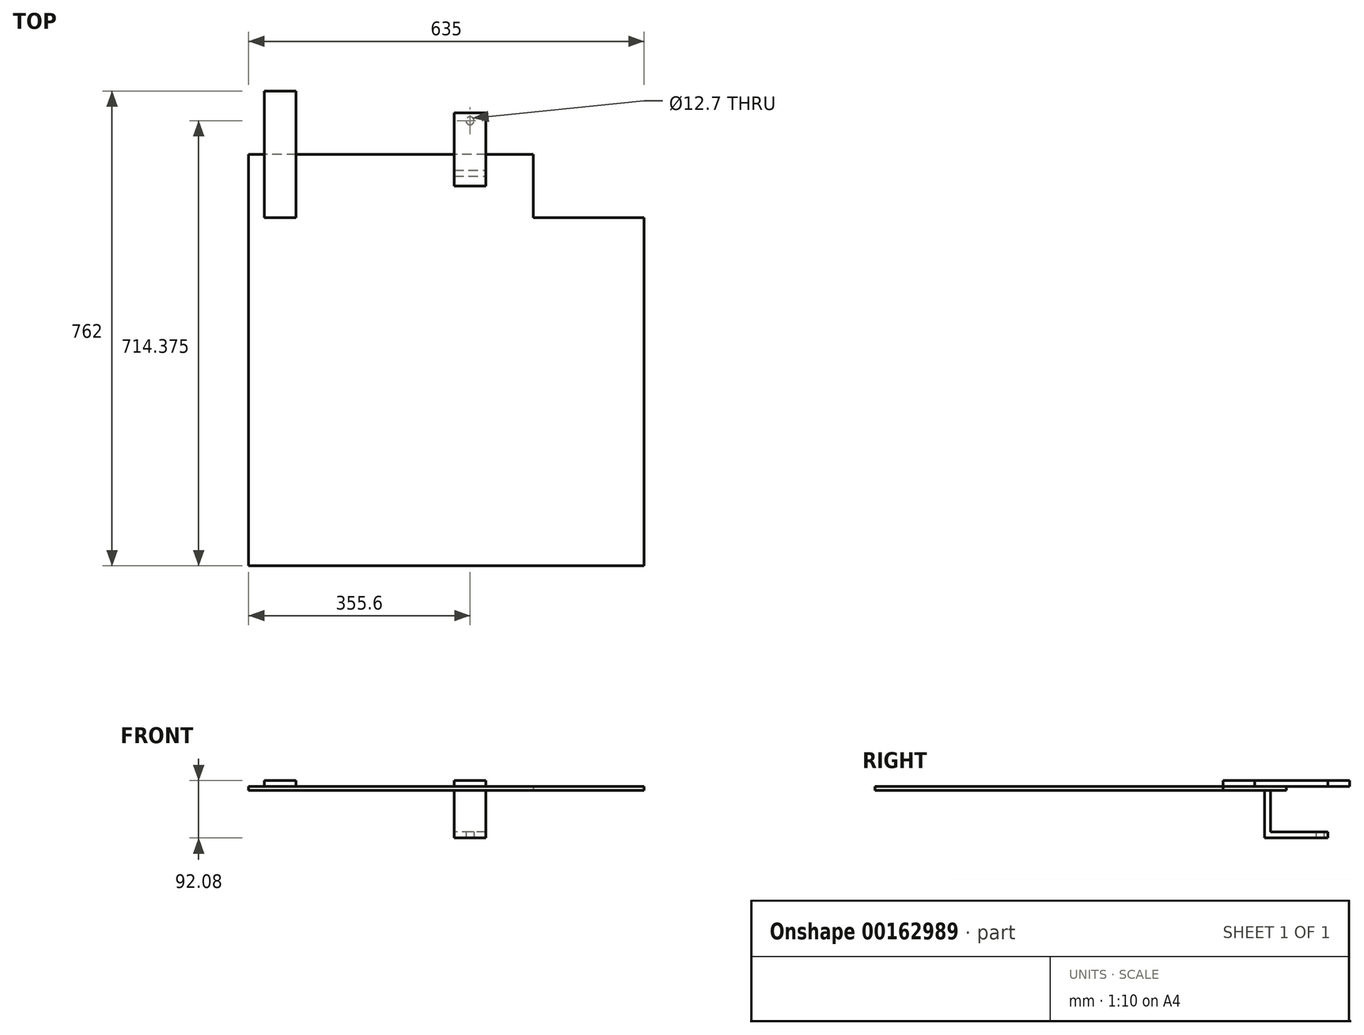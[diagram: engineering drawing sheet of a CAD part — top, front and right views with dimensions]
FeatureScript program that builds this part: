
annotation { "Feature Type Name" : "Feature", "Feature Type Description" : "" }
export const myFeature = defineFeature(function(context is Context, id is Id, definition is map)
    precondition{}
    {
        {
            var Q0;
            Q0=qCreatedBy(makeId("Top.planeOp"),FACE);
            var sketch = newSketch(context, id + "F0", { "sketchPlane" : qUnion([Q0])});
            skLineSegment(sketch, "E0.bottom", {"start": v(317.5, -330.2) * mm, "end": v(-317.5, -330.2) * mm});
            skLineSegment(sketch, "E0.top", {"start": v(139.7, 330.2) * mm, "end": v(-317.5, 330.2) * mm});
            skLineSegment(sketch, "E0.left", {"start": v(317.5, -330.2) * mm, "end": v(317.5, 228.6) * mm});
            skLineSegment(sketch, "E0.right", {"start": v(-317.5, -330.2) * mm, "end": v(-317.5, 330.2) * mm});
            skPoint(sketch, "E0.middle", {"position": v(0, 0) * mm});
            skLineSegment(sketch, "E1.top", {"start": v(317.5, 228.6) * mm, "end": v(139.7, 228.6) * mm});
            skLineSegment(sketch, "E1.right", {"start": v(139.7, 330.2) * mm, "end": v(139.7, 228.6) * mm});
            skPoint(sketch, "E2.orphan", {"position": v(317.5, 330.2) * mm});
            skSolve(sketch);
        }
        {
            var Q0;
            Q0=makeQuery(id+"F0.imprint","IMPRINT",FACE,{"disambiguationData":[TD([[makeQuery(id+"F0.imprint","IMPRINT",EDGE,{"derivedFrom":sQuery(id+"F0.wireOp",EDGE,"E0.bottom")}),-1.0]])]});
            extrude(context, id + "F1", {"entities" : qUnion([Q0]), "depth" : 6.35 * mm});
        }
        {
            var Q0;
            Q0=makeQuery(id+"F1.opExtrude","CAP_FACE",FACE,{"disambiguationData":[OSD([sQuery(id+"F0.wireOp",EDGE,"E0.bottom"),sQuery(id+"F0.wireOp",EDGE,"E0.top"),sQuery(id+"F0.wireOp",EDGE,"E0.left"),sQuery(id+"F0.wireOp",EDGE,"E0.right"),sQuery(id+"F0.wireOp",EDGE,"E1.top"),sQuery(id+"F0.wireOp",EDGE,"E1.right")])],"isStart":false});
            var sketch = newSketch(context, id + "F2", { "sketchPlane" : qUnion([Q0])});
            skLineSegment(sketch, "E3.bottom", {"start": v(-241.3, 228.6) * mm, "end": v(-292.1, 228.6) * mm});
            skLineSegment(sketch, "E3.top", {"start": v(-241.3, 431.8) * mm, "end": v(-292.1, 431.8) * mm});
            skLineSegment(sketch, "E3.left", {"start": v(-241.3, 228.6) * mm, "end": v(-241.3, 431.8) * mm});
            skLineSegment(sketch, "E3.right", {"start": v(-292.1, 228.6) * mm, "end": v(-292.1, 431.8) * mm});
            skPoint(sketch, "E3.middle", {"position": v(-266.7, 330.2) * mm});
            skSolve(sketch);
        }
        {
            var Q0;
            {var subQ0=sQuery(id+"F2.wireOp",EDGE,"E3.bottom");Q0=makeQuery(id+"F2.imprint","IMPRINT",FACE,{"disambiguationData":[TD([[makeQuery(id+"F2.imprint","IMPRINT",EDGE,{"derivedFrom":subQ0}),-1.0]])]});}
            var Q1;
            {var subQ0=sQuery(id+"F2.wireOp",EDGE,"E3.top");Q1=makeQuery(id+"F2.imprint","IMPRINT",FACE,{"disambiguationData":[TD([[makeQuery(id+"F2.imprint","IMPRINT",EDGE,{"derivedFrom":subQ0}),1.0]])]});}
            extrude(context, id + "F3", {"entities" : qUnion([Q0, Q1]), "operationType" : NewBodyOperationType.ADD, "depth" : 9.52 * mm});
        }
        {
            var Q0;
            Q0=makeQuery(id+"F1.opExtrude","CAP_FACE",FACE,{"disambiguationData":[OSD([sQuery(id+"F0.wireOp",EDGE,"E0.bottom"),sQuery(id+"F0.wireOp",EDGE,"E0.top"),sQuery(id+"F0.wireOp",EDGE,"E0.left"),sQuery(id+"F0.wireOp",EDGE,"E0.right"),sQuery(id+"F0.wireOp",EDGE,"E1.top"),sQuery(id+"F0.wireOp",EDGE,"E1.right")])],"isStart":true});
            var sketch = newSketch(context, id + "F4", { "sketchPlane" : qUnion([Q0])});
            skLineSegment(sketch, "E4.bottom", {"start": v(12.7, -295.28) * mm, "end": v(63.5, -295.28) * mm});
            skLineSegment(sketch, "E4.top", {"start": v(12.7, -304.8) * mm, "end": v(63.5, -304.8) * mm});
            skLineSegment(sketch, "E4.left", {"start": v(12.7, -295.28) * mm, "end": v(12.7, -304.8) * mm});
            skLineSegment(sketch, "E4.right", {"start": v(63.5, -295.28) * mm, "end": v(63.5, -304.8) * mm});
            skPoint(sketch, "E4.middle", {"position": v(38.1, -300.04) * mm});
            skSolve(sketch);
        }
        {
            var Q0;
            Q0=makeQuery(id+"F4.imprint","IMPRINT",FACE,{"disambiguationData":[TD([[makeQuery(id+"F4.imprint","IMPRINT",EDGE,{"derivedFrom":sQuery(id+"F4.wireOp",EDGE,"E4.bottom")}),-1.0]])]});
            extrude(context, id + "F5", {"entities" : qUnion([Q0]), "operationType" : NewBodyOperationType.ADD, "depth" : 76.2 * mm});
        }
        {
            var Q0;
            Q0=makeQuery(id+"F5.opExtrude","SWEPT_FACE",FACE,{"disambiguationData":[OSD([sQuery(id+"F4.wireOp",EDGE,"E4.top")])]});
            var sketch = newSketch(context, id + "F6", { "sketchPlane" : qUnion([Q0])});
            skLineSegment(sketch, "E5.bottom", {"start": v(-63.5, -76.2) * mm, "end": v(-12.7, -76.2) * mm});
            skLineSegment(sketch, "E5.top", {"start": v(-63.5, -66.68) * mm, "end": v(-12.7, -66.68) * mm});
            skLineSegment(sketch, "E5.left", {"start": v(-63.5, -76.2) * mm, "end": v(-63.5, -66.68) * mm});
            skLineSegment(sketch, "E5.right", {"start": v(-12.7, -76.2) * mm, "end": v(-12.7, -66.68) * mm});
            skSolve(sketch);
        }
        {
            var Q0;
            Q0=makeQuery(id+"F6.imprint","IMPRINT",FACE,{"disambiguationData":[TD([[makeQuery(id+"F6.imprint","IMPRINT",EDGE,{"derivedFrom":sQuery(id+"F6.wireOp",EDGE,"E5.bottom")}),-1.0]])]});
            extrude(context, id + "F7", {"entities" : qUnion([Q0]), "operationType" : NewBodyOperationType.ADD, "depth" : 92.07 * mm});
        }
        {
            var Q0;
            Q0=makeQuery(id+"F7.boolean.opBoolean","MERGE",FACE,{"derivedFrom":[makeQuery(id+"F5.opExtrude","CAP_FACE",FACE,{"disambiguationData":[OSD([sQuery(id+"F4.wireOp",EDGE,"E4.bottom"),sQuery(id+"F4.wireOp",EDGE,"E4.top"),sQuery(id+"F4.wireOp",EDGE,"E4.left"),sQuery(id+"F4.wireOp",EDGE,"E4.right")])],"isStart":false}),makeQuery(id+"F7.opExtrude","SWEPT_FACE",FACE,{"disambiguationData":[OSD([sQuery(id+"F6.wireOp",EDGE,"E5.bottom")])]})]});
            var sketch = newSketch(context, id + "F8", { "sketchPlane" : qUnion([Q0])});
            skCircle(sketch, "E6", {"center": v(38.1, -384.18) * mm, "radius": 6.35 * mm});
            skPoint(sketch, "E6.centerSnap0", {"position": v(38.1, -396.88) * mm});
            skSolve(sketch);
        }
        {
            var Q0;
            Q0=makeQuery(id+"F8.imprint","IMPRINT",FACE,{"disambiguationData":[TD([[makeQuery(id+"F8.imprint","IMPRINT",EDGE,{"derivedFrom":sQuery(id+"F8.wireOp",EDGE,"E6")}),1.0]])]});
            extrude(context, id + "F9", {"entities" : qUnion([Q0]), "operationType" : NewBodyOperationType.REMOVE, "oppositeDirection" : true, "depth" : 25.4 * mm});
        }
        {
            var Q0;
            Q0=makeQuery(id+"F1.opExtrude","CAP_FACE",FACE,{"disambiguationData":[OSD([sQuery(id+"F0.wireOp",EDGE,"E0.bottom"),sQuery(id+"F0.wireOp",EDGE,"E0.top"),sQuery(id+"F0.wireOp",EDGE,"E0.left"),sQuery(id+"F0.wireOp",EDGE,"E0.right"),sQuery(id+"F0.wireOp",EDGE,"E1.top"),sQuery(id+"F0.wireOp",EDGE,"E1.right")])],"isStart":false});
            var sketch = newSketch(context, id + "F10", { "sketchPlane" : qUnion([Q0])});
            skLineSegment(sketch, "E7.top", {"start": v(63.5, 406.4) * mm, "end": v(12.7, 406.4) * mm});
            skLineSegment(sketch, "E7.left", {"start": v(63.5, 279.4) * mm, "end": v(63.5, 406.4) * mm});
            skLineSegment(sketch, "E7.right", {"start": v(12.7, 279.4) * mm, "end": v(12.7, 406.4) * mm});
            skPoint(sketch, "E7.middle", {"position": v(38.1, 330.2) * mm});
            skLineSegment(sketch, "E8", {"start": v(12.7, 396.88) * mm, "end": v(63.5, 396.88) * mm});
            skLineSegment(sketch, "E9", {"start": v(12.7, 279.4) * mm, "end": v(63.5, 279.4) * mm});
            skPoint(sketch, "E7.bottom.end.orphan", {"position": v(12.7, 254) * mm});
            skPoint(sketch, "E10.orphan", {"position": v(63.5, 254) * mm});
            skPoint(sketch, "E11.orphan", {"position": v(12.7, 330.2) * mm});
            skPoint(sketch, "E12.end.orphan", {"position": v(63.5, 330.2) * mm});
            skSolve(sketch);
        }
        {
            var Q0;
            {var subQ0=sQuery(id+"F10.wireOp",EDGE,"E8");Q0=makeQuery(id+"F10.imprint","IMPRINT",FACE,{"disambiguationData":[TD([[makeQuery(id+"F10.imprint","IMPRINT",EDGE,{"derivedFrom":subQ0}),-1.0]])]});}
            var Q1;
            {var subQ0=sQuery(id+"F10.wireOp",EDGE,"E9");Q1=makeQuery(id+"F10.imprint","IMPRINT",FACE,{"disambiguationData":[TD([[makeQuery(id+"F10.imprint","IMPRINT",EDGE,{"derivedFrom":subQ0}),1.0]])]});}
            extrude(context, id + "F11", {"entities" : qUnion([Q0, Q1]), "operationType" : NewBodyOperationType.ADD, "depth" : 9.52 * mm});
        }
    });
